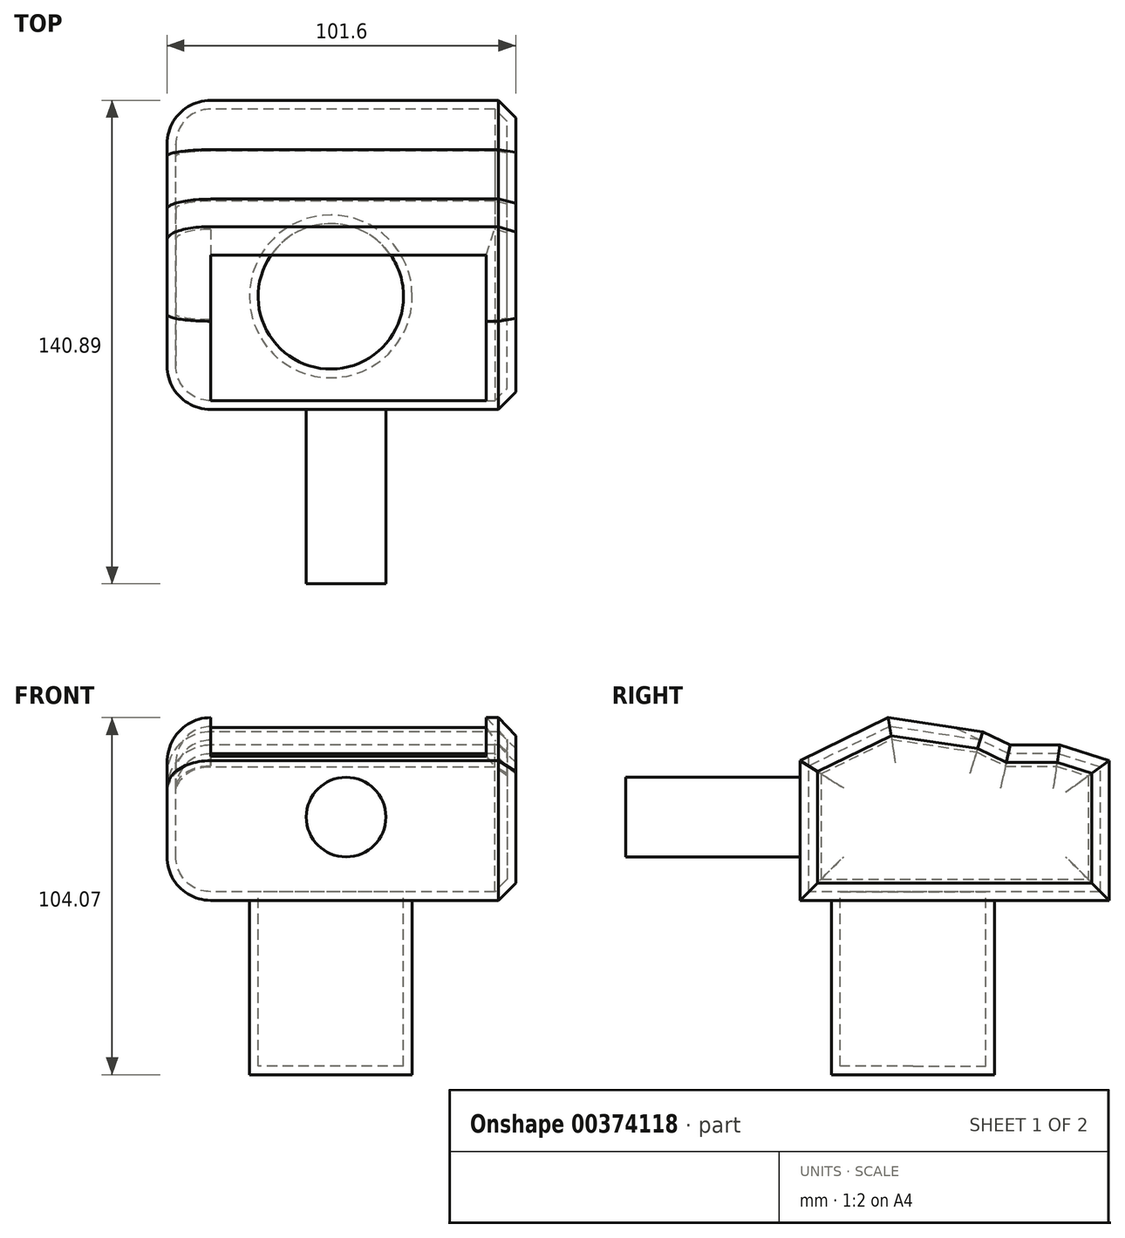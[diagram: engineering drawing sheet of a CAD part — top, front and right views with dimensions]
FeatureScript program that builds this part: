
annotation { "Feature Type Name" : "Feature", "Feature Type Description" : "" }
export const myFeature = defineFeature(function(context is Context, id is Id, definition is map)
    precondition{}
    {
        {
            var Q0;
            Q0=qCreatedBy(makeId("Right.planeOp"),FACE);
            var sketch = newSketch(context, id + "F0", { "sketchPlane" : qUnion([Q0])});
            skLineSegment(sketch, "E0.top", {"start": v(-112.9, 8.15) * mm, "end": v(-22.81, 8.15) * mm});
            skLineSegment(sketch, "E0.left", {"start": v(-112.9, 48.87) * mm, "end": v(-112.9, 8.15) * mm});
            skLineSegment(sketch, "E0.right", {"start": v(-22.81, 48.87) * mm, "end": v(-22.81, 8.15) * mm});
            skLineSegment(sketch, "E1", {"start": v(-112.9, 48.87) * mm, "end": v(-87.19, 61.42) * mm});
            skLineSegment(sketch, "E2", {"start": v(-87.19, 61.42) * mm, "end": v(-59.63, 57.3) * mm});
            skLineSegment(sketch, "E3", {"start": v(-59.63, 57.3) * mm, "end": v(-51.6, 53.4) * mm});
            skLineSegment(sketch, "E4", {"start": v(-51.6, 53.4) * mm, "end": v(-37.21, 53.4) * mm});
            skLineSegment(sketch, "E5", {"start": v(-37.21, 53.4) * mm, "end": v(-22.81, 48.87) * mm});
            skSolve(sketch);
        }
        {
            var Q0;
            Q0=makeQuery(id+"F0.imprint","IMPRINT",FACE,{"disambiguationData":[TD([[makeQuery(id+"F0.imprint","IMPRINT",EDGE,{"derivedFrom":sQuery(id+"F0.wireOp",EDGE,"E0.top")}),1.0]])]});
            extrude(context, id + "F1", {"entities" : qUnion([Q0]), "depth" : 101.6 * mm});
        }
        {
            var Q0;
            Q0=makeQuery(id+"F1.opExtrude","CAP_FACE",FACE,{"disambiguationData":[OSD([sQuery(id+"F0.wireOp",EDGE,"E0.top"),sQuery(id+"F0.wireOp",EDGE,"E0.left"),sQuery(id+"F0.wireOp",EDGE,"E0.right"),sQuery(id+"F0.wireOp",EDGE,"E1"),sQuery(id+"F0.wireOp",EDGE,"E2"),sQuery(id+"F0.wireOp",EDGE,"E3"),sQuery(id+"F0.wireOp",EDGE,"E4"),sQuery(id+"F0.wireOp",EDGE,"E5")])],"isStart":false});
            chamfer(context, id + "F2", {"entities" : qUnion([Q0]), "width" : 5.08 * mm, "tangentPropagation" : true});
        }
        {
            var Q0;
            Q0=makeQuery(id+"F1.opExtrude","CAP_FACE",FACE,{"disambiguationData":[OSD([sQuery(id+"F0.wireOp",EDGE,"E0.top"),sQuery(id+"F0.wireOp",EDGE,"E0.left"),sQuery(id+"F0.wireOp",EDGE,"E0.right"),sQuery(id+"F0.wireOp",EDGE,"E1"),sQuery(id+"F0.wireOp",EDGE,"E2"),sQuery(id+"F0.wireOp",EDGE,"E3"),sQuery(id+"F0.wireOp",EDGE,"E4"),sQuery(id+"F0.wireOp",EDGE,"E5")])],"isStart":true});
            fillet(context, id + "F3", {"entities" : qUnion([Q0]), "radius" : 12.7 * mm, "tangentPropagation" : true, "allowEdgeOverflow" : false});
        }
        {
            var Q0;
            Q0=makeQuery(id+"F1.opExtrude","SWEPT_FACE",FACE,{"disambiguationData":[OSD([sQuery(id+"F0.wireOp",EDGE,"E0.top")])]});
            var sketch = newSketch(context, id + "F4", { "sketchPlane" : qUnion([Q0])});
            skCircle(sketch, "E6", {"center": v(47.73, 79.95) * mm, "radius": 23.72 * mm});
            skSolve(sketch);
        }
        {
            var Q0;
            Q0=makeQuery(id+"F4.imprint","IMPRINT",FACE,{"disambiguationData":[TD([[makeQuery(id+"F4.imprint","IMPRINT",EDGE,{"derivedFrom":sQuery(id+"F4.wireOp",EDGE,"E6")}),1.0]])]});
            extrude(context, id + "F5", {"entities" : qUnion([Q0]), "operationType" : NewBodyOperationType.ADD, "depth" : 50.8 * mm});
        }
        {
            var Q0;
            Q0=makeQuery(id+"F1.opExtrude","SWEPT_FACE",FACE,{"disambiguationData":[OSD([sQuery(id+"F0.wireOp",EDGE,"E1")])]});
            var Q1;
            Q1=makeQuery(id+"F1.opExtrude","SWEPT_FACE",FACE,{"disambiguationData":[OSD([sQuery(id+"F0.wireOp",EDGE,"E2")])]});
            shell(context, id + "F6", {"entities" : qUnion([Q0, Q1]), "thickness" : 2.54 * mm});
        }
        {
            var Q0;
            Q0=makeQuery(id+"F1.opExtrude","SWEPT_FACE",FACE,{"disambiguationData":[OSD([sQuery(id+"F0.wireOp",EDGE,"E0.left")])]});
            var sketch = newSketch(context, id + "F7", { "sketchPlane" : qUnion([Q0])});
            skCircle(sketch, "E7", {"center": v(52.18, 32.42) * mm, "radius": 11.6 * mm});
            skSolve(sketch);
        }
        {
            var Q0;
            Q0=makeQuery(id+"F7.imprint","IMPRINT",FACE,{"disambiguationData":[TD([[makeQuery(id+"F7.imprint","IMPRINT",EDGE,{"derivedFrom":sQuery(id+"F7.wireOp",EDGE,"E7")}),1.0]])]});
            extrude(context, id + "F8", {"entities" : qUnion([Q0]), "operationType" : NewBodyOperationType.ADD, "depth" : 50.8 * mm});
        }
    });
